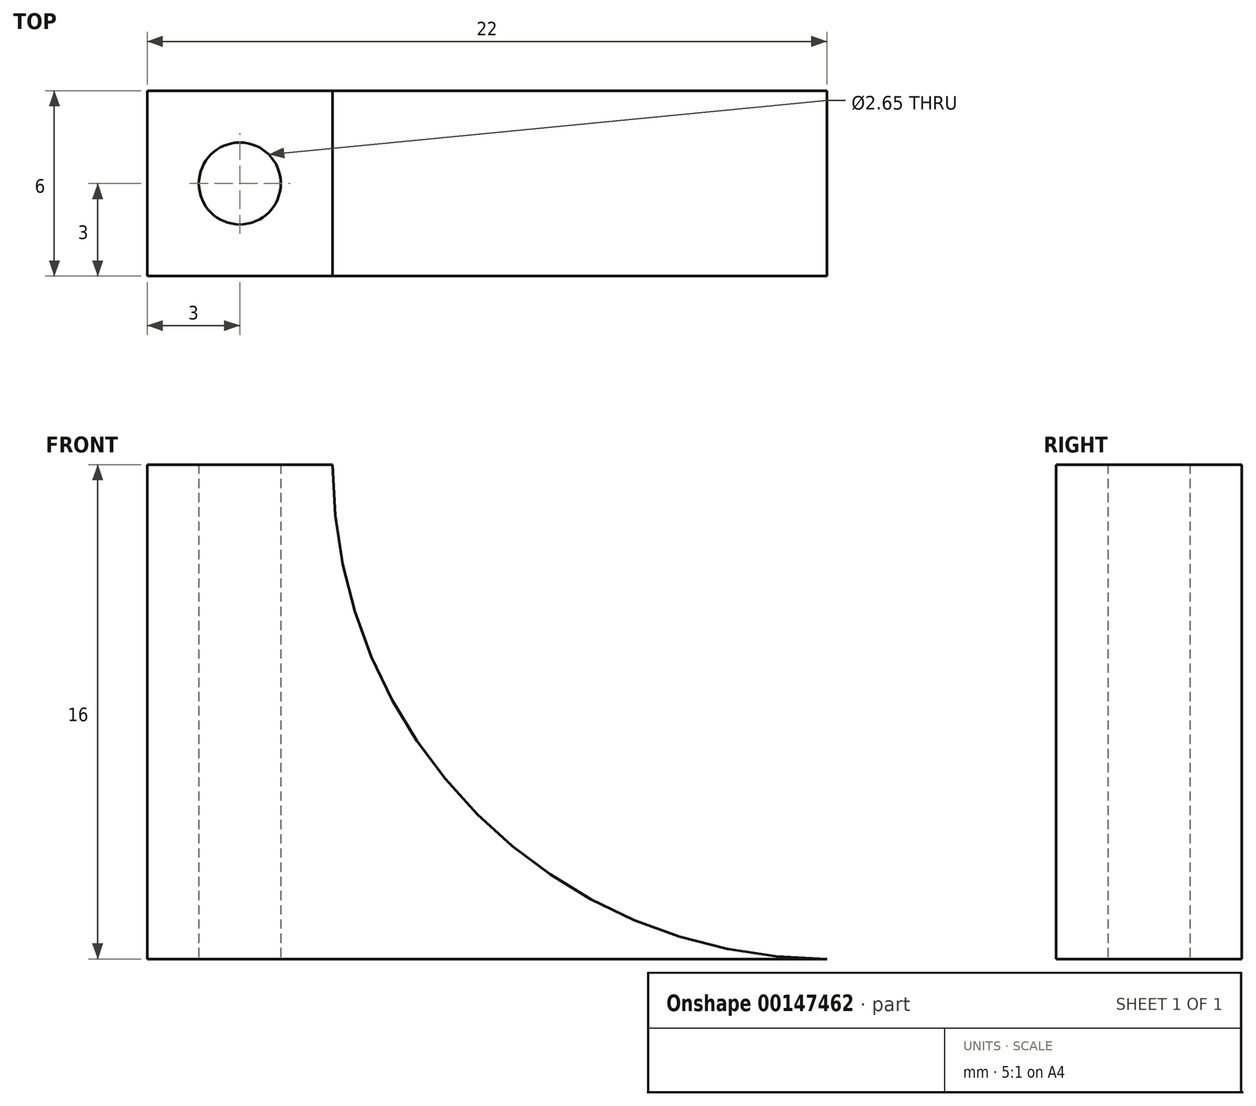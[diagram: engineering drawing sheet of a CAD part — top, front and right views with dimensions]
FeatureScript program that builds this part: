
annotation { "Feature Type Name" : "Feature", "Feature Type Description" : "" }
export const myFeature = defineFeature(function(context is Context, id is Id, definition is map)
    precondition{}
    {
        {
            var Q0;
            Q0=qCreatedBy(makeId("Top.planeOp"),FACE);
            var sketch = newSketch(context, id + "F0", { "sketchPlane" : qUnion([Q0])});
            skLineSegment(sketch, "E0.bottom", {"start": v(-11, 3) * mm, "end": v(11, 3) * mm});
            skLineSegment(sketch, "E0.top", {"start": v(-11, -3) * mm, "end": v(11, -3) * mm});
            skLineSegment(sketch, "E0.left", {"start": v(-11, 3) * mm, "end": v(-11, -3) * mm});
            skLineSegment(sketch, "E0.right", {"start": v(11, 3) * mm, "end": v(11, -3) * mm});
            skPoint(sketch, "E0.middle", {"position": v(0, 0) * mm});
            skLineSegment(sketch, "E1", {"start": v(0, 0) * mm, "end": v(-8, 0) * mm});
            skCircle(sketch, "E2", {"center": v(-8, 0) * mm, "radius": 1.32 * mm});
            skSolve(sketch);
        }
        {
            var Q0;
            Q0 = qSketchRegion(id + "F0", true);
            extrude(context, id + "F1", {"entities" : qUnion([Q0]), "depth" : 16 * mm});
        }
        {
            var Q0;
            Q0=qCreatedBy(makeId("Front.planeOp"),FACE);
            var sketch = newSketch(context, id + "F2", { "sketchPlane" : qUnion([Q0])});
            skLineSegment(sketch, "E3.bottom", {"start": v(0, 0) * mm, "end": v(11, 0) * mm, "construction": true});
            skLineSegment(sketch, "E3.top", {"start": v(0, 16) * mm, "end": v(11, 16) * mm, "construction": true});
            skLineSegment(sketch, "E3.left", {"start": v(0, 0) * mm, "end": v(0, 16) * mm, "construction": true});
            skLineSegment(sketch, "E3.right", {"start": v(11, 0) * mm, "end": v(11, 16) * mm, "construction": true});
            skCircle(sketch, "E4", {"center": v(11, 16) * mm, "radius": 16 * mm});
            skSolve(sketch);
        }
        {
            var Q0;
            Q0 = qSketchRegion(id + "F2", true);
            extrude(context, id + "F3", {"entities" : qUnion([Q0]), "operationType" : NewBodyOperationType.REMOVE, "endBound" : BoundingType.SYMMETRIC, "oppositeDirection" : true, "depth" : 10 * mm});
        }
    });
